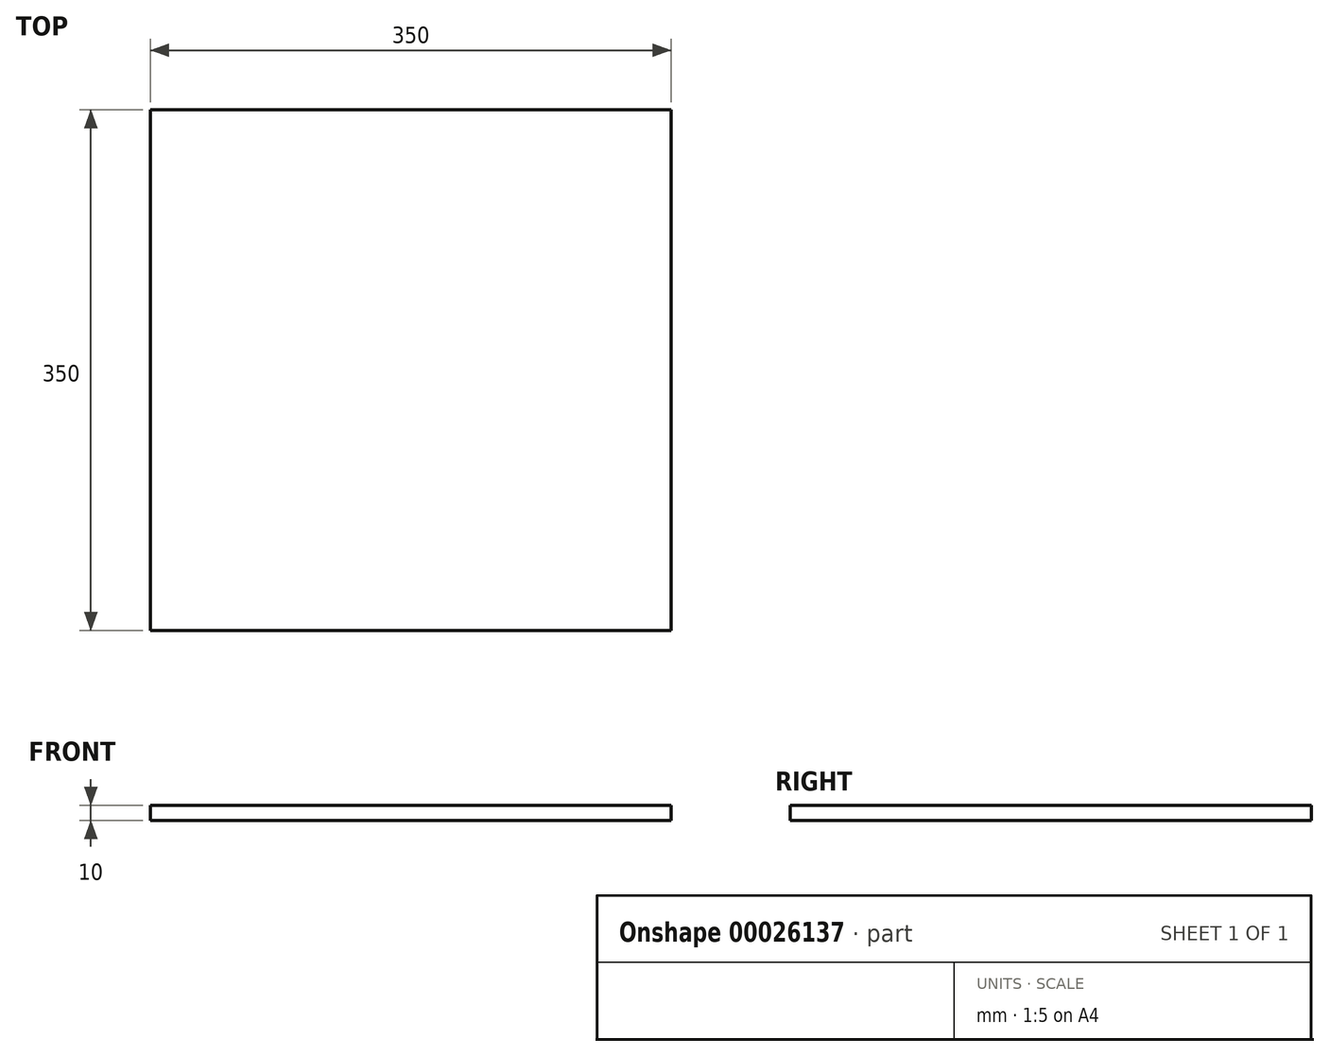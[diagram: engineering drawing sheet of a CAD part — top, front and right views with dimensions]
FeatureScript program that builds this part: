
annotation { "Feature Type Name" : "Feature", "Feature Type Description" : "" }
export const myFeature = defineFeature(function(context is Context, id is Id, definition is map)
    precondition{}
    {
        {
            var Q0;
            Q0=qCreatedBy(makeId("Top.planeOp"),FACE);
            var sketch = newSketch(context, id + "F0", { "sketchPlane" : qUnion([Q0])});
            skLineSegment(sketch, "E0.rect.bottom", {"start": v(175, 175) * mm, "end": v(-175, 175) * mm});
            skLineSegment(sketch, "E0.rect.top", {"start": v(175, -175) * mm, "end": v(-175, -175) * mm});
            skLineSegment(sketch, "E0.rect.left", {"start": v(175, 175) * mm, "end": v(175, -175) * mm});
            skLineSegment(sketch, "E0.rect.right", {"start": v(-175, 175) * mm, "end": v(-175, -175) * mm});
            skPoint(sketch, "E0.rect.middle", {"position": v(0, 0) * mm});
            skSolve(sketch);
        }
        {
            var Q0;
            Q0=makeQuery(id+"F0.imprint","IMPRINT",FACE,{"disambiguationData":[TD([[makeQuery(id+"F0.imprint","IMPRINT",EDGE,{"derivedFrom":sQuery(id+"F0.wireOp",EDGE,"E0.rect.bottom")}),1.0]])]});
            extrude(context, id + "F1", {"entities" : qUnion([Q0]), "depth" : 10 * mm});
        }
    });
